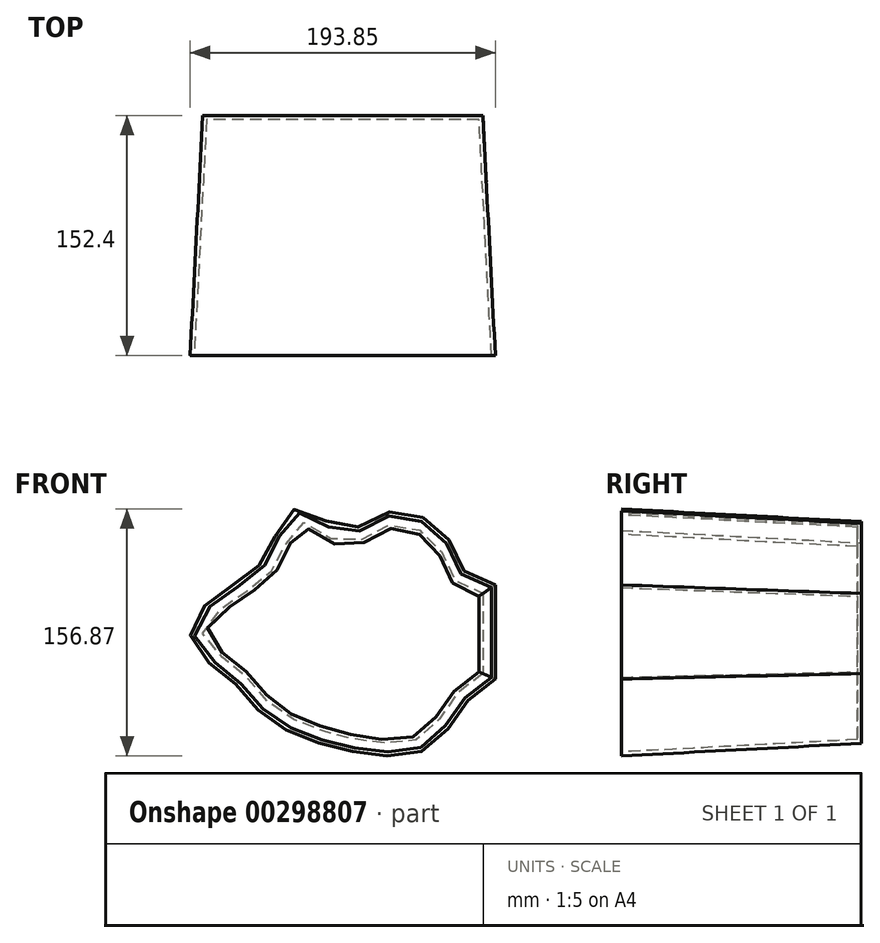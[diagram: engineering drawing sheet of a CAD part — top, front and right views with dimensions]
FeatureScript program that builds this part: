
annotation { "Feature Type Name" : "Feature", "Feature Type Description" : "" }
export const myFeature = defineFeature(function(context is Context, id is Id, definition is map)
    precondition{}
    {
        {
            var Q0;
            Q0=qCreatedBy(makeId("Front.planeOp"),FACE);
            var sketch = newSketch(context, id + "F0", { "sketchPlane" : qUnion([Q0])});
            skLineSegment(sketch, "E0.right", {"start": v(76.2, 25.4) * mm, "end": v(76.2, -25.4) * mm});
            skPoint(sketch, "E0.middle", {"position": v(0, 0) * mm});
            skPoint(sketch, "E1.visualSharp", {"position": v(-76.2, 50.8) * mm});
            skPoint(sketch, "E2.visualSharp", {"position": v(76.2, 50.8) * mm});
            skPoint(sketch, "E3.visualSharp", {"position": v(76.2, -50.8) * mm});
            skPoint(sketch, "E4.visualSharp", {"position": v(-76.2, -50.8) * mm});
            skFitSpline(sketch, "E5", {"points": [v(50.8, -50.8) * mm, v(31.06, -68.48) * mm, v(-50.8, -50.8) * mm, v(-76.2, -25.4) * mm, v(-101.66, 0) * mm, v(-76.2, 25.4) * mm, v(-50.8, 50.8) * mm, v(-41.42, 71.07) * mm, v(-11.06, 57.65) * mm, v(21.41, 69.9) * mm, v(50.8, 50.8) * mm, v(58.83, 33.65) * mm, v(76.2, 25.4) * mm, v(94.84, 9.18) * mm, v(76.2, -25.4) * mm, v(62.83, -35.3) * mm, v(50.8, -50.8) * mm]});
            skSolve(sketch);
        }
        {
            var Q0;
            {var subQ0=sQuery(id+"F0.wireOp",EDGE,"E0.right");Q0=makeQuery(id+"F0.imprint","IMPRINT",FACE,{"disambiguationData":[TD([[makeQuery(id+"F0.imprint","IMPRINT",EDGE,{"derivedFrom":subQ0}),-1.0]])]});}
            extrude(context, id + "F1", {"entities" : qUnion([Q0]), "depth" : 152.4 * mm, "hasDraft" : true, "draftAngle" : 3 * degree});
        }
        {
            var Q0;
            Q0=makeQuery(id+"F1.opExtrude","CAP_FACE",FACE,{"disambiguationData":[OSD([sQuery(id+"F0.wireOp",EDGE,"E0.right"),sQuery(id+"F0.wireOp",EDGE,"E5")])],"isStart":false});
            shell(context, id + "F2", {"entities" : qUnion([Q0]), "thickness" : 2.54 * mm});
        }
    });
